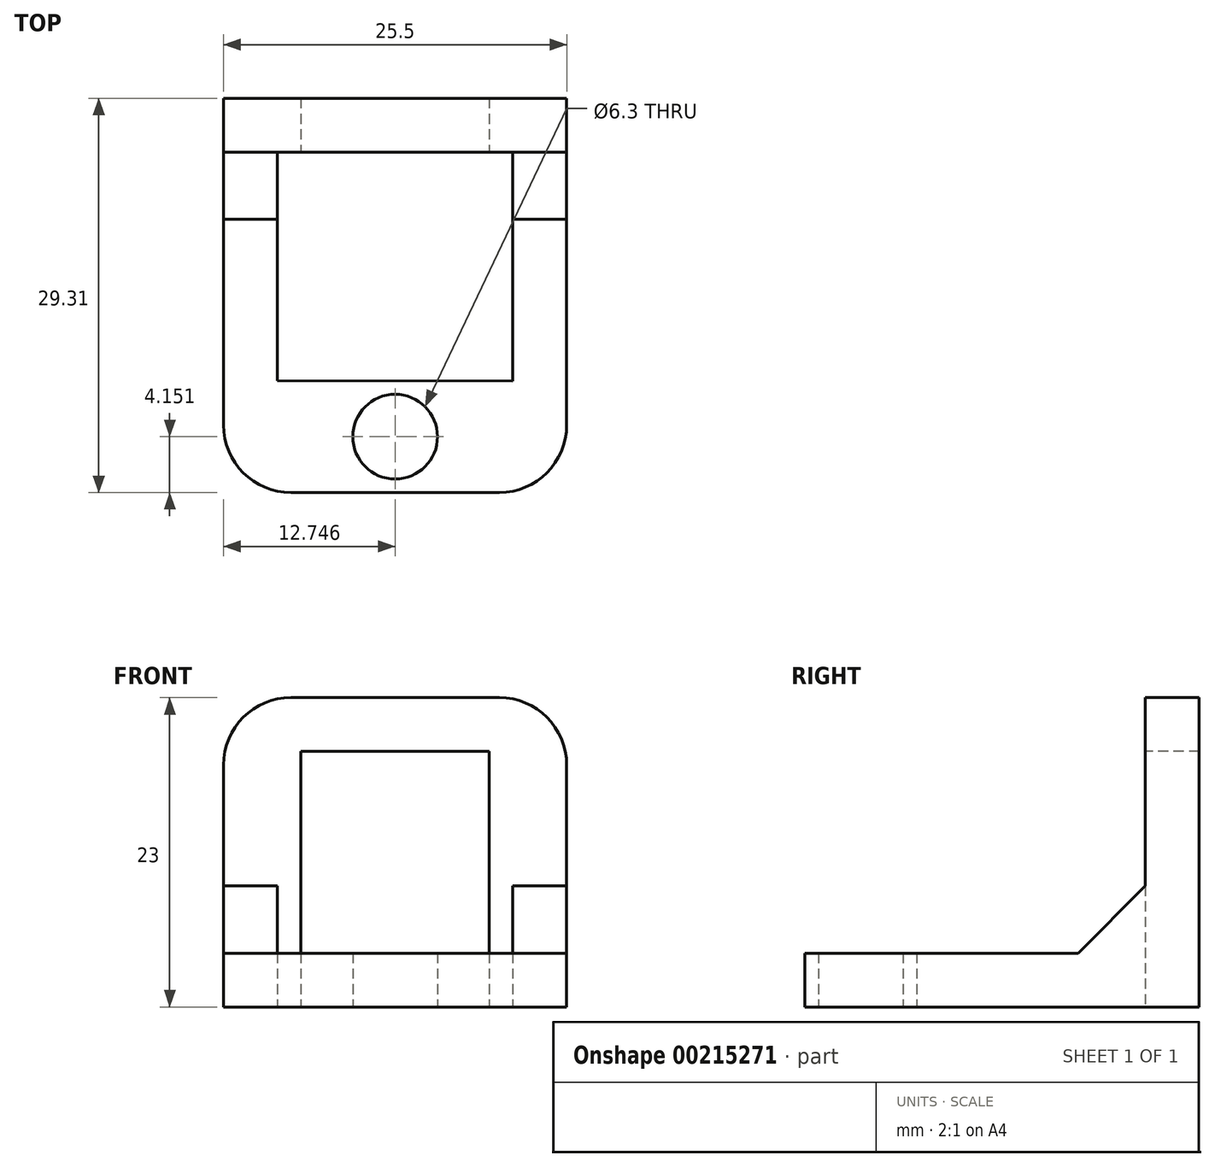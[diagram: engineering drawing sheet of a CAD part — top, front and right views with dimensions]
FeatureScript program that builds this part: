
annotation { "Feature Type Name" : "Feature", "Feature Type Description" : "" }
export const myFeature = defineFeature(function(context is Context, id is Id, definition is map)
    precondition{}
    {
        {
            assignVariable(context, id + "F0", {"name" : "thickness", "anyValue" : 4});
        }
        {
            var Q0;
            Q0=qCreatedBy(makeId("Top.planeOp"),FACE);
            var sketch = newSketch(context, id + "F1", { "sketchPlane" : qUnion([Q0])});
            skLineSegment(sketch, "E0.bottom", {"start": v(-10.2, 17.72) * mm, "end": v(-4.45, 17.72) * mm});
            skLineSegment(sketch, "E0.top", {"start": v(-10.2, -11.59) * mm, "end": v(15.3, -11.59) * mm});
            skLineSegment(sketch, "E0.left", {"start": v(-10.2, 17.72) * mm, "end": v(-10.2, -11.59) * mm});
            skLineSegment(sketch, "E0.right", {"start": v(15.3, 17.72) * mm, "end": v(15.3, -11.59) * mm});
            skLineSegment(sketch, "E1", {"start": v(-10.2, 13.72) * mm, "end": v(-3.95, 13.72) * mm});
            skLineSegment(sketch, "E2", {"start": v(-4.45, 17.72) * mm, "end": v(-4.45, 13.72) * mm});
            skPoint(sketch, "E3", {"position": v(2.55, -11.59) * mm});
            skCircle(sketch, "E4", {"center": v(2.55, -7.44) * mm, "radius": 3.15 * mm});
            skLineSegment(sketch, "E5", {"start": v(9.55, 17.72) * mm, "end": v(15.3, 17.72) * mm});
            skLineSegment(sketch, "E6", {"start": v(-3.95, 13.72) * mm, "end": v(9.55, 13.72) * mm});
            skLineSegment(sketch, "E7", {"start": v(9.55, 13.72) * mm, "end": v(15.3, 13.72) * mm});
            skLineSegment(sketch, "E8", {"start": v(9.55, 17.72) * mm, "end": v(9.55, 13.72) * mm});
            skLineSegment(sketch, "E9", {"start": v(11.3, 13.72) * mm, "end": v(11.3, -3.3) * mm});
            skLineSegment(sketch, "E10", {"start": v(-6.2, -3.28) * mm, "end": v(-6.2, 13.72) * mm});
            skPoint(sketch, "E11", {"position": v(2.8, 13.72) * mm});
            skLineSegment(sketch, "E12", {"start": v(-4.45, 17.72) * mm, "end": v(9.55, 17.72) * mm});
            skLineSegment(sketch, "E13", {"start": v(-6.2, -3.28) * mm, "end": v(11.3, -3.3) * mm});
            skPoint(sketch, "E14", {"position": v(2.55, 17.72) * mm});
            skPoint(sketch, "E15", {"position": v(2.55, -3.29) * mm});
            skSolve(sketch);
        }
        {
            var Q0;
            Q0=makeQuery(id+"F1.imprint","IMPRINT",FACE,{"disambiguationData":[TD([[makeQuery(id+"F1.imprint","IMPRINT",EDGE,{"derivedFrom":sQuery(id+"F1.wireOp",EDGE,"E0.bottom")}),-1.0]])]});
            var Q1;
            {var subQ13=sQuery(id+"F1.wireOp",EDGE,"E0.top");Q1=makeQuery(id+"F1.imprint","IMPRINT",FACE,{"disambiguationData":[TD([[makeQuery(id+"F1.imprint","IMPRINT",EDGE,{"derivedFrom":subQ13}),1.0]])]});}
            var Q2;
            {var subQ5=sQuery(id+"F1.wireOp",EDGE,"tsaf94wI-5ksy-pZcB-9BJk-sPMIc3kGAQw0");Q2=makeQuery(id+"F1.imprint","IMPRINT",FACE,{"disambiguationData":[TD([[makeQuery(id+"F1.imprint","IMPRINT",EDGE,{"derivedFrom":subQ5}),1.0]])]});}
            var Q3;
            {var subQ5=sQuery(id+"F1.wireOp",EDGE,"yuCnrXNv-5jOn-PrJZ-vSMY-qbwhfnYQ3npa");Q3=makeQuery(id+"F1.imprint","IMPRINT",FACE,{"disambiguationData":[TD([[makeQuery(id+"F1.imprint","IMPRINT",EDGE,{"derivedFrom":subQ5}),1.0]])]});}
            var Q4;
            {var subQ0=sQuery(id+"F1.wireOp",EDGE,"E2");var subQ1=sQuery(id+"F1.wireOp",EDGE,"E1");var subQ2=makeQuery(id+"F1.imprint","INTERSECT",VERTEX,{"derivedFrom":[subQ1,subQ0]});Q4=makeQuery(id+"F1.imprint","IMPRINT",FACE,{"disambiguationData":[TD([[makeQuery(id+"F1.imprint","IMPRINT",EDGE,{"disambiguationData":[TD([[subQ2,-1.0]])],"derivedFrom":subQ1}),1.0]])]});}
            var Q5;
            {var subQ0=sQuery(id+"F1.wireOp",EDGE,"XrT7I5yw-Ebxo-LcNd-WIcs-2V9b3E7o4qho");var subQ1=sQuery(id+"F1.wireOp",EDGE,"E1");var subQ2=makeQuery(id+"F1.imprint","INTERSECT",VERTEX,{"derivedFrom":[subQ1,subQ0]});Q5=makeQuery(id+"F1.imprint","IMPRINT",FACE,{"disambiguationData":[TD([[makeQuery(id+"F1.imprint","IMPRINT",EDGE,{"disambiguationData":[TD([[subQ2,-1.0]])],"derivedFrom":subQ1}),1.0]])]});}
            var Q6;
            {var subQ0=sQuery(id+"F1.wireOp",EDGE,"ThOInSl4-wMf3-Xs07-aqWu-xJaj1eAhEU5E");var subQ1=sQuery(id+"F1.wireOp",EDGE,"E1");var subQ2=makeQuery(id+"F1.imprint","INTERSECT",VERTEX,{"derivedFrom":[subQ1,subQ0]});Q6=makeQuery(id+"F1.imprint","IMPRINT",FACE,{"disambiguationData":[TD([[makeQuery(id+"F1.imprint","IMPRINT",EDGE,{"disambiguationData":[TD([[subQ2,-1.0]])],"derivedFrom":subQ1}),1.0]])]});}
            var Q7;
            {var subQ0=sQuery(id+"F1.wireOp",EDGE,"E5");Q7=makeQuery(id+"F1.imprint","IMPRINT",FACE,{"disambiguationData":[TD([[makeQuery(id+"F1.imprint","IMPRINT",EDGE,{"derivedFrom":subQ0}),-1.0]])]});}
            extrude(context, id + "F2", {"entities" : qUnion([Q0, Q1, Q2, Q3, Q4, Q5, Q6, Q7]), "depth" : 4 * mm});
        }
        {
            var Q0;
            {var subQ0=sQuery(id+"F1.wireOp",EDGE,"E0.left");var subQ1=sQuery(id+"F1.wireOp",EDGE,"E0.bottom");var subQ2=makeQuery(id+"F1.imprint","INTERSECT",VERTEX,{"derivedFrom":[subQ1,subQ0]});Q0=makeQuery(id+"F1.imprint","IMPRINT",FACE,{"disambiguationData":[TD([[makeQuery(id+"F1.imprint","IMPRINT",EDGE,{"disambiguationData":[TD([[subQ2,-1.0]])],"derivedFrom":subQ1}),-1.0]])]});}
            var Q1;
            {var subQ0=sQuery(id+"F1.wireOp",EDGE,"E2");var subQ1=sQuery(id+"F1.wireOp",EDGE,"E0.bottom");var subQ2=makeQuery(id+"F1.imprint","INTERSECT",VERTEX,{"derivedFrom":[subQ1,subQ0]});Q1=makeQuery(id+"F1.imprint","IMPRINT",FACE,{"disambiguationData":[TD([[makeQuery(id+"F1.imprint","IMPRINT",EDGE,{"disambiguationData":[TD([[subQ2,-1.0]])],"derivedFrom":subQ1}),-1.0]])]});}
            var Q2;
            {var subQ0=sQuery(id+"F1.wireOp",EDGE,"XrT7I5yw-Ebxo-LcNd-WIcs-2V9b3E7o4qho");var subQ1=sQuery(id+"F1.wireOp",EDGE,"E0.bottom");var subQ2=makeQuery(id+"F1.imprint","INTERSECT",VERTEX,{"derivedFrom":[subQ1,subQ0]});Q2=makeQuery(id+"F1.imprint","IMPRINT",FACE,{"disambiguationData":[TD([[makeQuery(id+"F1.imprint","IMPRINT",EDGE,{"disambiguationData":[TD([[subQ2,-1.0]])],"derivedFrom":subQ1}),-1.0]])]});}
            var Q3;
            {var subQ0=sQuery(id+"F1.wireOp",EDGE,"ThOInSl4-wMf3-Xs07-aqWu-xJaj1eAhEU5E");var subQ1=sQuery(id+"F1.wireOp",EDGE,"E0.bottom");var subQ2=makeQuery(id+"F1.imprint","INTERSECT",VERTEX,{"derivedFrom":[subQ1,subQ0]});Q3=makeQuery(id+"F1.imprint","IMPRINT",FACE,{"disambiguationData":[TD([[makeQuery(id+"F1.imprint","IMPRINT",EDGE,{"disambiguationData":[TD([[subQ2,-1.0]])],"derivedFrom":subQ1}),-1.0]])]});}
            var Q4;
            {var subQ0=sQuery(id+"F1.wireOp",EDGE,"E0.right");var subQ1=sQuery(id+"F1.wireOp",EDGE,"E0.bottom");var subQ2=makeQuery(id+"F1.imprint","INTERSECT",VERTEX,{"derivedFrom":[subQ1,subQ0]});Q4=makeQuery(id+"F1.imprint","IMPRINT",FACE,{"disambiguationData":[TD([[makeQuery(id+"F1.imprint","IMPRINT",EDGE,{"disambiguationData":[TD([[subQ2,1.0]])],"derivedFrom":subQ1}),-1.0]])]});}
            var Q5;
            {var subQ0=sQuery(id+"F1.wireOp",EDGE,"E2");var subQ1=sQuery(id+"F1.wireOp",EDGE,"E1");var subQ2=makeQuery(id+"F1.imprint","INTERSECT",VERTEX,{"derivedFrom":[subQ1,subQ0]});Q5=makeQuery(id+"F1.imprint","IMPRINT",FACE,{"disambiguationData":[TD([[makeQuery(id+"F1.imprint","IMPRINT",EDGE,{"disambiguationData":[TD([[subQ2,-1.0]])],"derivedFrom":subQ1}),1.0]])]});}
            var Q6;
            {var subQ0=sQuery(id+"F1.wireOp",EDGE,"XrT7I5yw-Ebxo-LcNd-WIcs-2V9b3E7o4qho");var subQ1=sQuery(id+"F1.wireOp",EDGE,"E1");var subQ2=makeQuery(id+"F1.imprint","INTERSECT",VERTEX,{"derivedFrom":[subQ1,subQ0]});Q6=makeQuery(id+"F1.imprint","IMPRINT",FACE,{"disambiguationData":[TD([[makeQuery(id+"F1.imprint","IMPRINT",EDGE,{"disambiguationData":[TD([[subQ2,-1.0]])],"derivedFrom":subQ1}),1.0]])]});}
            var Q7;
            {var subQ0=sQuery(id+"F1.wireOp",EDGE,"ThOInSl4-wMf3-Xs07-aqWu-xJaj1eAhEU5E");var subQ1=sQuery(id+"F1.wireOp",EDGE,"E1");var subQ2=makeQuery(id+"F1.imprint","INTERSECT",VERTEX,{"derivedFrom":[subQ1,subQ0]});Q7=makeQuery(id+"F1.imprint","IMPRINT",FACE,{"disambiguationData":[TD([[makeQuery(id+"F1.imprint","IMPRINT",EDGE,{"disambiguationData":[TD([[subQ2,-1.0]])],"derivedFrom":subQ1}),1.0]])]});}
            var Q8;
            {var subQ0=sQuery(id+"F1.wireOp",EDGE,"E5");Q8=makeQuery(id+"F1.imprint","IMPRINT",FACE,{"disambiguationData":[TD([[makeQuery(id+"F1.imprint","IMPRINT",EDGE,{"derivedFrom":subQ0}),-1.0]])]});}
            var Q9;
            Q9=makeQuery(id+"F1.imprint","IMPRINT",FACE,{"disambiguationData":[TD([[makeQuery(id+"F1.imprint","IMPRINT",EDGE,{"derivedFrom":sQuery(id+"F1.wireOp",EDGE,"0fe1addc-4afa-4ea3-9c5b-f0af2351ea85")}),-1.0]])]});
            var Q10;
            Q10=makeQuery(id+"F1.imprint","IMPRINT",FACE,{"disambiguationData":[TD([[makeQuery(id+"F1.imprint","IMPRINT",EDGE,{"derivedFrom":sQuery(id+"F1.wireOp",EDGE,"E6")}),1.0]])]});
            extrude(context, id + "F3", {"entities" : qUnion([Q0, Q1, Q2, Q3, Q4, Q5, Q6, Q7, Q8, Q9, Q10]), "operationType" : NewBodyOperationType.ADD, "depth" : (2 * getVariable(context, 'thickness') + 15) * mm});
        }
        {
            var Q0;
            {var subQ5=sQuery(id+"F1.wireOp",EDGE,"tsaf94wI-5ksy-pZcB-9BJk-sPMIc3kGAQw0");Q0=makeQuery(id+"F1.imprint","IMPRINT",FACE,{"disambiguationData":[TD([[makeQuery(id+"F1.imprint","IMPRINT",EDGE,{"derivedFrom":subQ5}),1.0]])]});}
            var Q1;
            {var subQ5=sQuery(id+"F1.wireOp",EDGE,"yuCnrXNv-5jOn-PrJZ-vSMY-qbwhfnYQ3npa");Q1=makeQuery(id+"F1.imprint","IMPRINT",FACE,{"disambiguationData":[TD([[makeQuery(id+"F1.imprint","IMPRINT",EDGE,{"derivedFrom":subQ5}),1.0]])]});}
            var Q2;
            {var subQ0=sQuery(id+"F1.wireOp",EDGE,"E2");var subQ1=sQuery(id+"F1.wireOp",EDGE,"E1");var subQ2=makeQuery(id+"F1.imprint","INTERSECT",VERTEX,{"derivedFrom":[subQ1,subQ0]});Q2=makeQuery(id+"F1.imprint","IMPRINT",FACE,{"disambiguationData":[TD([[makeQuery(id+"F1.imprint","IMPRINT",EDGE,{"disambiguationData":[TD([[subQ2,-1.0]])],"derivedFrom":subQ1}),1.0]])]});}
            var Q3;
            Q3=makeQuery(id+"F1.imprint","IMPRINT",FACE,{"disambiguationData":[TD([[makeQuery(id+"F1.imprint","IMPRINT",EDGE,{"derivedFrom":sQuery(id+"F1.wireOp",EDGE,"E6")}),1.0]])]});
            extrude(context, id + "F4", {"entities" : qUnion([Q0, Q1, Q2, Q3]), "operationType" : NewBodyOperationType.REMOVE, "depth" : (getVariable(context, 'thickness') + 15) * mm});
        }
        {
            var Q0;
            Q0=makeQuery(id+"F2.opExtrude","SWEPT_EDGE",EDGE,{"disambiguationData":[OSD([sQuery(id+"F1.wireOp",EDGE,"E0.top"),sQuery(id+"F1.wireOp",EDGE,"E0.left")])]});
            var Q1;
            Q1=makeQuery(id+"F2.opExtrude","SWEPT_EDGE",EDGE,{"disambiguationData":[OSD([sQuery(id+"F1.wireOp",EDGE,"E0.top"),sQuery(id+"F1.wireOp",EDGE,"E0.right")])]});
            var Q2;
            Q2=makeQuery(id+"F3.opExtrude","CAP_EDGE",EDGE,{"disambiguationData":[OSD([sQuery(id+"F1.wireOp",EDGE,"E0.right")])],"isStart":false});
            var Q3;
            Q3=makeQuery(id+"F3.opExtrude","CAP_EDGE",EDGE,{"disambiguationData":[OSD([sQuery(id+"F1.wireOp",EDGE,"E0.left")])],"isStart":false});
            fillet(context, id + "F5", {"entities" : qUnion([Q0, Q1, Q2, Q3]), "radius" : 5 * mm, "tangentPropagation" : true, "allowEdgeOverflow" : false});
        }
        {
            var Q0;
            {var subQ0=sQuery(id+"F1.wireOp",EDGE,"E7");var subQ1=sQuery(id+"F1.wireOp",EDGE,"E6");var subQ2=sQuery(id+"F1.wireOp",EDGE,"E1");Q0=makeQuery(id+"F3.boolean.opBoolean","INTERSECT",EDGE,{"disambiguationData":[OD(1.0)],"derivedFrom":[makeQuery(id+"F2.opExtrude","CAP_FACE",FACE,{"disambiguationData":[OSD([sQuery(id+"F1.wireOp",EDGE,"E0.bottom"),sQuery(id+"F1.wireOp",EDGE,"E0.top"),sQuery(id+"F1.wireOp",EDGE,"E0.left"),sQuery(id+"F1.wireOp",EDGE,"E0.right"),subQ2,sQuery(id+"F1.wireOp",EDGE,"E4"),sQuery(id+"F1.wireOp",EDGE,"E5"),subQ1,subQ0,sQuery(id+"F1.wireOp",EDGE,"E9"),sQuery(id+"F1.wireOp",EDGE,"E10"),sQuery(id+"F1.wireOp",EDGE,"E12"),sQuery(id+"F1.wireOp",EDGE,"E13")])],"isStart":false}),makeQuery(id+"F3.opExtrude","SWEPT_FACE",FACE,{"disambiguationData":[OSD([subQ2,subQ1,subQ0])]})]});}
            var Q1;
            {var subQ0=sQuery(id+"F1.wireOp",EDGE,"E7");var subQ1=sQuery(id+"F1.wireOp",EDGE,"E6");var subQ2=sQuery(id+"F1.wireOp",EDGE,"E1");Q1=makeQuery(id+"F3.boolean.opBoolean","INTERSECT",EDGE,{"disambiguationData":[OD(0.0)],"derivedFrom":[makeQuery(id+"F2.opExtrude","CAP_FACE",FACE,{"disambiguationData":[OSD([sQuery(id+"F1.wireOp",EDGE,"E0.bottom"),sQuery(id+"F1.wireOp",EDGE,"E0.top"),sQuery(id+"F1.wireOp",EDGE,"E0.left"),sQuery(id+"F1.wireOp",EDGE,"E0.right"),subQ2,sQuery(id+"F1.wireOp",EDGE,"E4"),sQuery(id+"F1.wireOp",EDGE,"E5"),subQ1,subQ0,sQuery(id+"F1.wireOp",EDGE,"E9"),sQuery(id+"F1.wireOp",EDGE,"E10"),sQuery(id+"F1.wireOp",EDGE,"E12"),sQuery(id+"F1.wireOp",EDGE,"E13")])],"isStart":false}),makeQuery(id+"F3.opExtrude","SWEPT_FACE",FACE,{"disambiguationData":[OSD([subQ2,subQ1,subQ0])]})]});}
            chamfer(context, id + "F6", {"entities" : qUnion([Q0, Q1]), "width" : 5 * mm, "tangentPropagation" : true});
        }
    });
